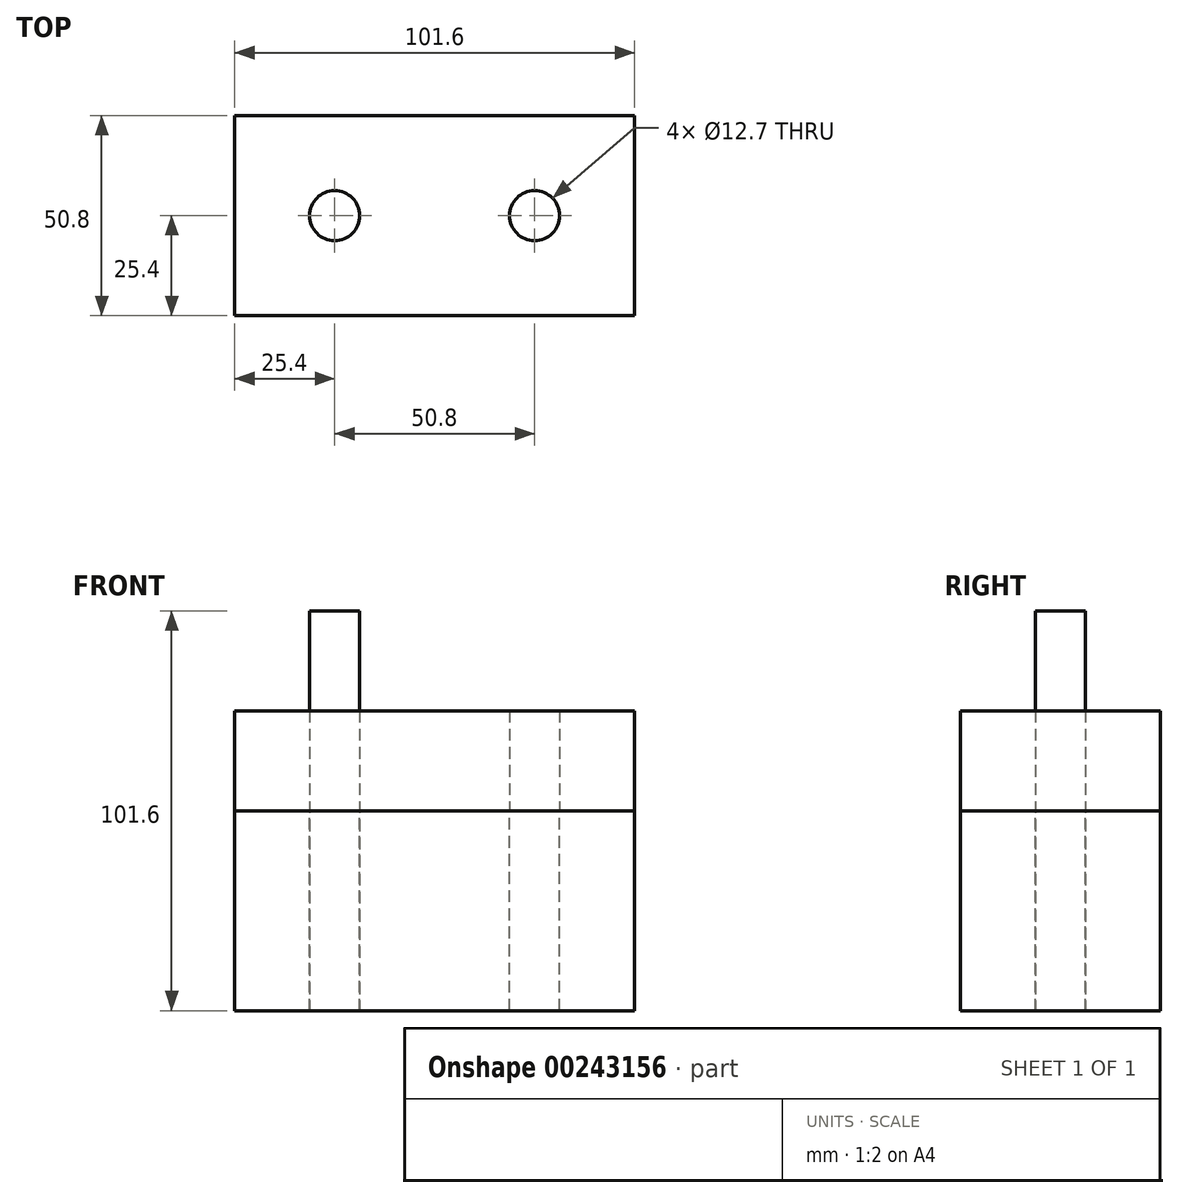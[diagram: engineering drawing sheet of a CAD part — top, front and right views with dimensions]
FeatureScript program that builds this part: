
annotation { "Feature Type Name" : "Feature", "Feature Type Description" : "" }
export const myFeature = defineFeature(function(context is Context, id is Id, definition is map)
    precondition{}
    {
        {
            var Q0;
            Q0=qCreatedBy(makeId("Top.planeOp"),FACE);
            var sketch = newSketch(context, id + "F0", { "sketchPlane" : qUnion([Q0])});
            skLineSegment(sketch, "E0.bottom", {"start": v(0, 0) * mm, "end": v(101.6, 0) * mm});
            skLineSegment(sketch, "E0.top", {"start": v(0, 50.8) * mm, "end": v(101.6, 50.8) * mm});
            skLineSegment(sketch, "E0.left", {"start": v(0, 0) * mm, "end": v(0, 50.8) * mm});
            skLineSegment(sketch, "E0.right", {"start": v(101.6, 0) * mm, "end": v(101.6, 50.8) * mm});
            skCircle(sketch, "E1", {"center": v(25.4, 25.4) * mm, "radius": 6.35 * mm});
            skCircle(sketch, "E2", {"center": v(76.2, 25.4) * mm, "radius": 6.35 * mm});
            skSolve(sketch);
        }
        {
            var Q0;
            Q0=makeQuery(id+"F0.imprint","IMPRINT",FACE,{"disambiguationData":[TD([[makeQuery(id+"F0.imprint","IMPRINT",EDGE,{"derivedFrom":sQuery(id+"F0.wireOp",EDGE,"E0.bottom")}),1.0]])]});
            extrude(context, id + "F1", {"entities" : qUnion([Q0]), "depth" : 25.4 * mm});
        }
        {
            var Q0;
            Q0=makeQuery(id+"F1.opExtrude","CAP_FACE",FACE,{"disambiguationData":[OSD([sQuery(id+"F0.wireOp",EDGE,"E0.bottom"),sQuery(id+"F0.wireOp",EDGE,"E0.top"),sQuery(id+"F0.wireOp",EDGE,"E0.left"),sQuery(id+"F0.wireOp",EDGE,"E0.right"),sQuery(id+"F0.wireOp",EDGE,"E1"),sQuery(id+"F0.wireOp",EDGE,"E2")])],"isStart":true});
            extrude(context, id + "F2", {"entities" : qUnion([Q0]), "depth" : 50.8 * mm});
        }
        {
            var Q0;
            Q0=makeQuery(id+"F2.opExtrude","CAP_FACE",FACE,{"disambiguationData":[OSD([sQuery(id+"F0.wireOp",EDGE,"E0.bottom"),sQuery(id+"F0.wireOp",EDGE,"E0.top"),sQuery(id+"F0.wireOp",EDGE,"E0.left"),sQuery(id+"F0.wireOp",EDGE,"E0.right"),sQuery(id+"F0.wireOp",EDGE,"E1"),sQuery(id+"F0.wireOp",EDGE,"E2")])],"isStart":false});
            var sketch = newSketch(context, id + "F3", { "sketchPlane" : qUnion([Q0])});
            skCircle(sketch, "E3", {"center": v(25.4, -25.4) * mm, "radius": 6.35 * mm});
            skSolve(sketch);
        }
        {
            var Q0;
            Q0 = qSketchRegion(id + "F3", true);
            extrude(context, id + "F4", {"entities" : qUnion([Q0]), "oppositeDirection" : true, "depth" : 101.6 * mm});
        }
    });
